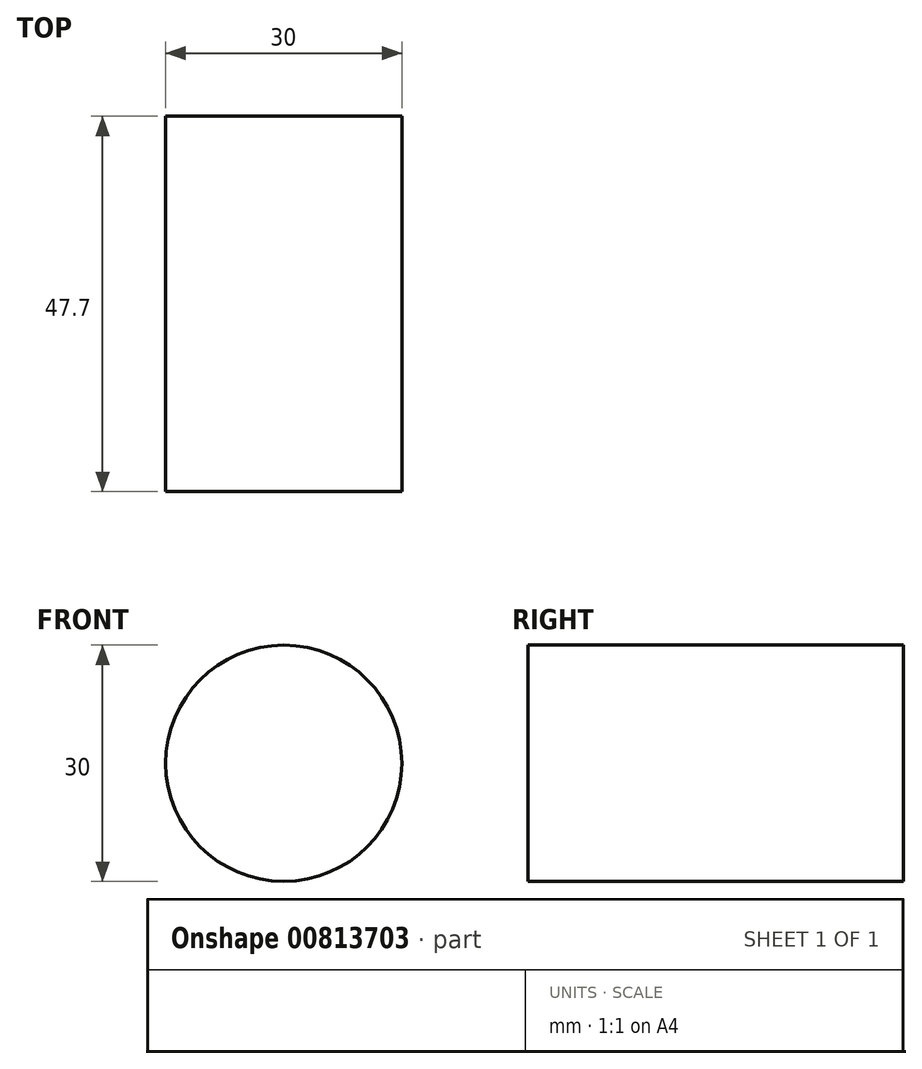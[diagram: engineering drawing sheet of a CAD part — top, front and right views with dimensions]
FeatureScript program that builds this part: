
annotation { "Feature Type Name" : "Feature", "Feature Type Description" : "" }
export const myFeature = defineFeature(function(context is Context, id is Id, definition is map)
    precondition{}
    {
        {
            var Q0;
            Q0=qCreatedBy(makeId("Front.planeOp"),FACE);
            var sketch = newSketch(context, id + "F0", { "sketchPlane" : qUnion([Q0])});
            skCircle(sketch, "E0", {"center": v(0, 0) * mm, "radius": 15 * mm});
            skSolve(sketch);
        }
        {
            var Q0;
            Q0=makeQuery(id+"F0.imprint","IMPRINT",FACE,{"disambiguationData":[TD([[makeQuery(id+"F0.imprint","IMPRINT",EDGE,{"derivedFrom":sQuery(id+"F0.wireOp",EDGE,"E0")}),1.0]])]});
            extrude(context, id + "F1", {"entities" : qUnion([Q0]), "depth" : 47.7 * mm, "offsetDistance" : 25 * mm});
        }
    });
